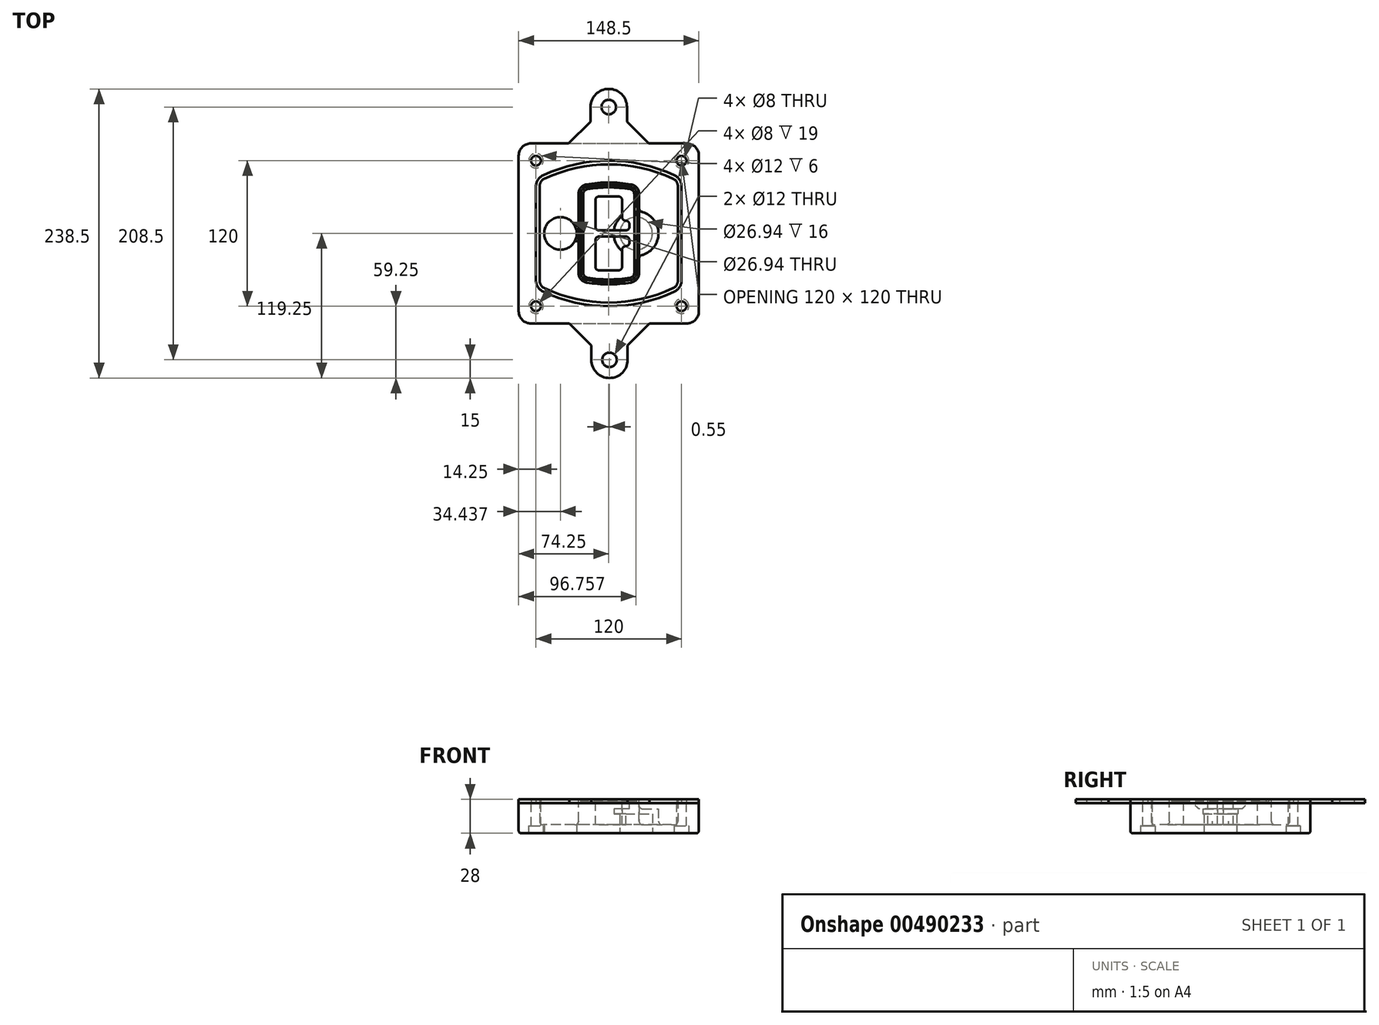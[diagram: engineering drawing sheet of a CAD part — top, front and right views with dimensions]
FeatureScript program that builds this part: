
annotation { "Feature Type Name" : "Feature", "Feature Type Description" : "" }
export const myFeature = defineFeature(function(context is Context, id is Id, definition is map)
    precondition{}
    {
        {
            var Q0;
            Q0=qCreatedBy(makeId("Top.planeOp"),FACE);
            var sketch = newSketch(context, id + "F0", { "sketchPlane" : qUnion([Q0])});
            skPoint(sketch, "E0.rect.middle", {"position": v(0, 0) * mm});
            skLineSegment(sketch, "E1.bottom", {"start": v(-64.25, -74.25) * mm, "end": v(64.25, -74.25) * mm});
            skLineSegment(sketch, "E1.top", {"start": v(-64.25, 74.25) * mm, "end": v(64.25, 74.25) * mm});
            skLineSegment(sketch, "E1.left", {"start": v(-74.25, -64.25) * mm, "end": v(-74.25, 64.25) * mm});
            skLineSegment(sketch, "E1.right", {"start": v(74.25, -64.25) * mm, "end": v(74.25, 64.25) * mm});
            skLineSegment(sketch, "E2", {"start": v(-74.25, 74.25) * mm, "end": v(74.25, -74.25) * mm, "construction": true});
            skLineSegment(sketch, "E3", {"start": v(74.25, 74.25) * mm, "end": v(-74.25, -74.25) * mm, "construction": true});
            skCircle(sketch, "E4", {"center": v(-60, 60) * mm, "radius": 4 * mm});
            skCircle(sketch, "E5", {"center": v(60, 60) * mm, "radius": 4 * mm});
            skCircle(sketch, "E6", {"center": v(60, -60) * mm, "radius": 4 * mm});
            skCircle(sketch, "E7", {"center": v(-60, -60) * mm, "radius": 4 * mm});
            skLineSegment(sketch, "E8", {"start": v(-60, 60) * mm, "end": v(60, 60) * mm, "construction": true});
            skLineSegment(sketch, "E9", {"start": v(60, 60) * mm, "end": v(60, -60) * mm, "construction": true});
            skLineSegment(sketch, "E10", {"start": v(60, -60) * mm, "end": v(-60, -60) * mm, "construction": true});
            skLineSegment(sketch, "E11", {"start": v(-60, -60) * mm, "end": v(-60, 60) * mm, "construction": true});
            skLineSegment(sketch, "E12", {"start": v(-60, 38.83) * mm, "end": v(-60, -38.83) * mm});
            skLineSegment(sketch, "E13", {"start": v(60, 38.83) * mm, "end": v(60, -38.83) * mm});
            skArc(sketch, "E14", {"start": v(54.26, 47.88) * mm, "mid": v(0, 60) * mm, "end": v(-54.26, 47.88) * mm});
            skArc(sketch, "E15", {"start": v(-54.26, -47.88) * mm, "mid": v(0, -60) * mm, "end": v(54.26, -47.88) * mm});
            skLineSegment(sketch, "E16", {"start": v(-60, 0) * mm, "end": v(60, 0) * mm, "construction": true});
            skPoint(sketch, "E17.visualSharp", {"position": v(-60, -45) * mm});
            skArc(sketch, "E17.filletArc", {"start": v(-60, -38.83) * mm, "mid": v(-58.44, -44.2) * mm, "end": v(-54.26, -47.88) * mm});
            skPoint(sketch, "E18.visualSharp", {"position": v(-60, 45) * mm});
            skArc(sketch, "E18.filletArc", {"start": v(-54.26, 47.88) * mm, "mid": v(-58.44, 44.2) * mm, "end": v(-60, 38.83) * mm});
            skPoint(sketch, "E19.visualSharp", {"position": v(60, 45) * mm});
            skArc(sketch, "E19.filletArc", {"start": v(60, 38.83) * mm, "mid": v(58.44, 44.2) * mm, "end": v(54.26, 47.88) * mm});
            skPoint(sketch, "E20.visualSharp", {"position": v(60, -45) * mm});
            skArc(sketch, "E20.filletArc", {"start": v(54.26, -47.88) * mm, "mid": v(58.44, -44.2) * mm, "end": v(60, -38.83) * mm});
            skPoint(sketch, "E21.visualSharp", {"position": v(-74.25, 74.25) * mm});
            skArc(sketch, "E21.filletArc", {"start": v(-64.25, 74.25) * mm, "mid": v(-71.32, 71.32) * mm, "end": v(-74.25, 64.25) * mm});
            skPoint(sketch, "E22.visualSharp", {"position": v(74.25, 74.25) * mm});
            skArc(sketch, "E22.filletArc", {"start": v(74.25, 64.25) * mm, "mid": v(71.32, 71.32) * mm, "end": v(64.25, 74.25) * mm});
            skPoint(sketch, "E23.visualSharp", {"position": v(74.25, -74.25) * mm});
            skArc(sketch, "E23.filletArc", {"start": v(64.25, -74.25) * mm, "mid": v(71.32, -71.32) * mm, "end": v(74.25, -64.25) * mm});
            skPoint(sketch, "E24.visualSharp", {"position": v(-74.25, -74.25) * mm});
            skArc(sketch, "E24.filletArc", {"start": v(-74.25, -64.25) * mm, "mid": v(-71.32, -71.32) * mm, "end": v(-64.25, -74.25) * mm});
            skArc(sketch, "E25.0", {"start": v(57, 38.83) * mm, "mid": v(55.9, 42.58) * mm, "end": v(52.98, 45.17) * mm});
            skLineSegment(sketch, "E25.1", {"start": v(57, 38.83) * mm, "end": v(57, -38.83) * mm});
            skArc(sketch, "E25.2", {"start": v(52.98, -45.17) * mm, "mid": v(55.9, -42.58) * mm, "end": v(57, -38.83) * mm});
            skArc(sketch, "E25.3", {"start": v(-52.98, -45.17) * mm, "mid": v(0, -57) * mm, "end": v(52.98, -45.17) * mm});
            skArc(sketch, "E25.4", {"start": v(-57, -38.83) * mm, "mid": v(-55.9, -42.58) * mm, "end": v(-52.98, -45.17) * mm});
            skArc(sketch, "E25.5", {"start": v(52.98, 45.17) * mm, "mid": v(0, 57) * mm, "end": v(-52.98, 45.17) * mm});
            skLineSegment(sketch, "E25.6", {"start": v(-57, 38.83) * mm, "end": v(-57, -38.83) * mm});
            skArc(sketch, "E25.7", {"start": v(-52.98, 45.17) * mm, "mid": v(-55.9, 42.58) * mm, "end": v(-57, 38.83) * mm});
            skArc(sketch, "E26.0", {"start": v(-55.96, 51.5) * mm, "mid": v(-61.82, 46.33) * mm, "end": v(-64, 38.83) * mm});
            skArc(sketch, "E26.1", {"start": v(55.96, 51.5) * mm, "mid": v(0, 64) * mm, "end": v(-55.96, 51.5) * mm});
            skArc(sketch, "E26.2", {"start": v(64, 38.83) * mm, "mid": v(61.82, 46.33) * mm, "end": v(55.96, 51.5) * mm});
            skLineSegment(sketch, "E26.3", {"start": v(64, 38.83) * mm, "end": v(64, -38.83) * mm});
            skArc(sketch, "E26.4", {"start": v(55.96, -51.5) * mm, "mid": v(61.82, -46.33) * mm, "end": v(64, -38.83) * mm});
            skLineSegment(sketch, "E26.5", {"start": v(-64, 38.83) * mm, "end": v(-64, -38.83) * mm});
            skArc(sketch, "E26.6", {"start": v(-55.96, -51.5) * mm, "mid": v(0, -64) * mm, "end": v(55.96, -51.5) * mm});
            skArc(sketch, "E26.7", {"start": v(-64, -38.83) * mm, "mid": v(-61.82, -46.33) * mm, "end": v(-55.96, -51.5) * mm});
            skSolve(sketch);
        }
        {
            var Q0;
            Q0=makeQuery(id+"F0.imprint","IMPRINT",FACE,{"disambiguationData":[TD([[makeQuery(id+"F0.imprint","IMPRINT",EDGE,{"derivedFrom":sQuery(id+"F0.wireOp",EDGE,"E1.bottom")}),1.0]])]});
            var Q1;
            Q1=makeQuery(id+"F0.imprint","IMPRINT",FACE,{"disambiguationData":[TD([[makeQuery(id+"F0.imprint","IMPRINT",EDGE,{"derivedFrom":sQuery(id+"F0.wireOp",EDGE,"E12")}),1.0]])]});
            var Q2;
            Q2=makeQuery(id+"F0.imprint","IMPRINT",FACE,{"disambiguationData":[TD([[makeQuery(id+"F0.imprint","IMPRINT",EDGE,{"derivedFrom":sQuery(id+"F0.wireOp",EDGE,"E25.0")}),1.0]])]});
            var Q3;
            Q3=makeQuery(id+"F0.imprint","IMPRINT",FACE,{"disambiguationData":[TD([[makeQuery(id+"F0.imprint","IMPRINT",EDGE,{"derivedFrom":sQuery(id+"F0.wireOp",EDGE,"E12")}),-1.0]])]});
            extrude(context, id + "F1", {"entities" : qUnion([Q0, Q1, Q2, Q3]), "oppositeDirection" : true, "depth" : 25 * mm});
        }
        {
            var Q0;
            Q0=makeQuery(id+"F0.imprint","IMPRINT",FACE,{"disambiguationData":[TD([[makeQuery(id+"F0.imprint","IMPRINT",EDGE,{"derivedFrom":sQuery(id+"F0.wireOp",EDGE,"E12")}),1.0]])]});
            extrude(context, id + "F2", {"entities" : qUnion([Q0]), "operationType" : NewBodyOperationType.ADD, "depth" : 3 * mm});
        }
        {
            var Q0;
            Q0=makeQuery(id+"F0.imprint","IMPRINT",FACE,{"disambiguationData":[TD([[makeQuery(id+"F0.imprint","IMPRINT",EDGE,{"derivedFrom":sQuery(id+"F0.wireOp",EDGE,"E25.0")}),1.0]])]});
            extrude(context, id + "F3", {"entities" : qUnion([Q0]), "operationType" : NewBodyOperationType.REMOVE, "oppositeDirection" : true, "depth" : 18 * mm});
        }
        {
            var Q0;
            Q0=makeQuery(id+"F2.opExtrude","CAP_FACE",FACE,{"disambiguationData":[OSD([sQuery(id+"F0.wireOp",EDGE,"E12"),sQuery(id+"F0.wireOp",EDGE,"E13"),sQuery(id+"F0.wireOp",EDGE,"E14"),sQuery(id+"F0.wireOp",EDGE,"E15"),sQuery(id+"F0.wireOp",EDGE,"E17.filletArc"),sQuery(id+"F0.wireOp",EDGE,"E18.filletArc"),sQuery(id+"F0.wireOp",EDGE,"E19.filletArc"),sQuery(id+"F0.wireOp",EDGE,"E20.filletArc"),sQuery(id+"F0.wireOp",EDGE,"E25.0"),sQuery(id+"F0.wireOp",EDGE,"E25.1"),sQuery(id+"F0.wireOp",EDGE,"E25.2"),sQuery(id+"F0.wireOp",EDGE,"E25.3"),sQuery(id+"F0.wireOp",EDGE,"E25.4"),sQuery(id+"F0.wireOp",EDGE,"E25.5"),sQuery(id+"F0.wireOp",EDGE,"E25.6"),sQuery(id+"F0.wireOp",EDGE,"E25.7")])],"isStart":false});
            var sketch = newSketch(context, id + "F4", { "sketchPlane" : qUnion([Q0])});
            skArc(sketch, "E27.0", {"start": v(-18.34, -40.45) * mm, "mid": v(0, -42) * mm, "end": v(18.34, -40.45) * mm});
            skArc(sketch, "E28.0", {"start": v(18.34, 40.45) * mm, "mid": v(0, 42) * mm, "end": v(-18.34, 40.45) * mm});
            skLineSegment(sketch, "E29", {"start": v(-25, 32.57) * mm, "end": v(-25, -32.57) * mm});
            skLineSegment(sketch, "E30", {"start": v(25, 32.57) * mm, "end": v(25, -32.57) * mm});
            skLineSegment(sketch, "E31", {"start": v(-25, 39.1) * mm, "end": v(25, 39.1) * mm, "construction": true});
            skLineSegment(sketch, "E32", {"start": v(-25, -39.1) * mm, "end": v(25, -39.1) * mm, "construction": true});
            skPoint(sketch, "E33.visualSharp", {"position": v(-25, 39.1) * mm});
            skArc(sketch, "E33.filletArc", {"start": v(-18.34, 40.45) * mm, "mid": v(-23.11, 37.73) * mm, "end": v(-25, 32.57) * mm});
            skPoint(sketch, "E34.visualSharp", {"position": v(25, 39.1) * mm});
            skArc(sketch, "E34.filletArc", {"start": v(25, 32.57) * mm, "mid": v(23.11, 37.73) * mm, "end": v(18.34, 40.45) * mm});
            skPoint(sketch, "E35.visualSharp", {"position": v(25, -39.1) * mm});
            skArc(sketch, "E35.filletArc", {"start": v(18.34, -40.45) * mm, "mid": v(23.11, -37.73) * mm, "end": v(25, -32.57) * mm});
            skPoint(sketch, "E36.visualSharp", {"position": v(-25, -39.1) * mm});
            skArc(sketch, "E36.filletArc", {"start": v(-25, -32.57) * mm, "mid": v(-23.11, -37.73) * mm, "end": v(-18.34, -40.45) * mm});
            skArc(sketch, "E37.0", {"start": v(52.98, 45.17) * mm, "mid": v(0, 57) * mm, "end": v(-52.98, 45.17) * mm});
            skArc(sketch, "E37.1", {"start": v(-52.98, 45.17) * mm, "mid": v(-55.9, 42.58) * mm, "end": v(-57, 38.83) * mm});
            skLineSegment(sketch, "E37.2", {"start": v(-57, 38.83) * mm, "end": v(-57, -38.83) * mm});
            skArc(sketch, "E37.3", {"start": v(-57, -38.83) * mm, "mid": v(-55.9, -42.58) * mm, "end": v(-52.98, -45.17) * mm});
            skArc(sketch, "E37.4", {"start": v(-52.98, -45.17) * mm, "mid": v(0, -57) * mm, "end": v(52.98, -45.17) * mm});
            skArc(sketch, "E37.5", {"start": v(52.98, -45.17) * mm, "mid": v(55.9, -42.58) * mm, "end": v(57, -38.83) * mm});
            skLineSegment(sketch, "E37.6", {"start": v(57, 38.83) * mm, "end": v(57, -38.83) * mm});
            skArc(sketch, "E37.7", {"start": v(57, 38.83) * mm, "mid": v(55.9, 42.58) * mm, "end": v(52.98, 45.17) * mm});
            skLineSegment(sketch, "E38.0", {"start": v(23, 32.57) * mm, "end": v(23, -32.57) * mm});
            skArc(sketch, "E38.1", {"start": v(18, -38.48) * mm, "mid": v(21.58, -36.44) * mm, "end": v(23, -32.57) * mm});
            skArc(sketch, "E38.2", {"start": v(-18, -38.48) * mm, "mid": v(0, -40) * mm, "end": v(18, -38.48) * mm});
            skArc(sketch, "E38.3", {"start": v(-23, -32.57) * mm, "mid": v(-21.58, -36.44) * mm, "end": v(-18, -38.48) * mm});
            skLineSegment(sketch, "E38.4", {"start": v(-23, 32.57) * mm, "end": v(-23, -32.57) * mm});
            skArc(sketch, "E38.5", {"start": v(23, 32.57) * mm, "mid": v(21.58, 36.44) * mm, "end": v(18, 38.48) * mm});
            skArc(sketch, "E38.6", {"start": v(-18, 38.48) * mm, "mid": v(-21.58, 36.44) * mm, "end": v(-23, 32.57) * mm});
            skArc(sketch, "E38.7", {"start": v(18, 38.48) * mm, "mid": v(0, 40) * mm, "end": v(-18, 38.48) * mm});
            skArc(sketch, "E39.0", {"start": v(21, 32.57) * mm, "mid": v(20.06, 35.15) * mm, "end": v(17.67, 36.5) * mm});
            skLineSegment(sketch, "E39.1", {"start": v(21, 32.57) * mm, "end": v(21, -32.57) * mm});
            skArc(sketch, "E39.2", {"start": v(17.67, -36.5) * mm, "mid": v(20.06, -35.15) * mm, "end": v(21, -32.57) * mm});
            skArc(sketch, "E39.3", {"start": v(-17.67, -36.5) * mm, "mid": v(0, -38) * mm, "end": v(17.67, -36.5) * mm});
            skArc(sketch, "E39.4", {"start": v(-21, -32.57) * mm, "mid": v(-20.06, -35.15) * mm, "end": v(-17.67, -36.5) * mm});
            skArc(sketch, "E39.5", {"start": v(17.67, 36.5) * mm, "mid": v(0, 38) * mm, "end": v(-17.67, 36.5) * mm});
            skLineSegment(sketch, "E39.6", {"start": v(-21, 32.57) * mm, "end": v(-21, -32.57) * mm});
            skArc(sketch, "E39.7", {"start": v(-17.67, 36.5) * mm, "mid": v(-20.06, 35.15) * mm, "end": v(-21, 32.57) * mm});
            skLineSegment(sketch, "E40", {"start": v(-25, 0) * mm, "end": v(25, 0) * mm, "construction": true});
            skLineSegment(sketch, "E41", {"start": v(-11, 5.5) * mm, "end": v(-11, 27.5) * mm});
            skLineSegment(sketch, "E42", {"start": v(-8, 30.5) * mm, "end": v(8, 30.5) * mm});
            skLineSegment(sketch, "E43", {"start": v(11, 27.5) * mm, "end": v(11, 13.5) * mm});
            skLineSegment(sketch, "E44", {"start": v(14, 10.5) * mm, "end": v(14, 10.5) * mm});
            skLineSegment(sketch, "E45", {"start": v(17, 7.5) * mm, "end": v(17, 5.5) * mm});
            skLineSegment(sketch, "E46", {"start": v(14, 2.5) * mm, "end": v(-8, 2.5) * mm});
            skPoint(sketch, "E47.visualSharp", {"position": v(-11, 30.5) * mm});
            skArc(sketch, "E47.filletArc", {"start": v(-8, 30.5) * mm, "mid": v(-10.12, 29.62) * mm, "end": v(-11, 27.5) * mm});
            skPoint(sketch, "E48.visualSharp", {"position": v(11, 30.5) * mm});
            skArc(sketch, "E48.filletArc", {"start": v(11, 27.5) * mm, "mid": v(10.12, 29.62) * mm, "end": v(8, 30.5) * mm});
            skPoint(sketch, "E49.visualSharp", {"position": v(11, 10.5) * mm});
            skArc(sketch, "E49.filletArc", {"start": v(11, 13.5) * mm, "mid": v(11.88, 11.38) * mm, "end": v(14, 10.5) * mm});
            skPoint(sketch, "E50.visualSharp", {"position": v(17, 10.5) * mm});
            skArc(sketch, "E50.filletArc", {"start": v(17, 7.5) * mm, "mid": v(16.12, 9.62) * mm, "end": v(14, 10.5) * mm});
            skPoint(sketch, "E51.visualSharp", {"position": v(17, 2.5) * mm});
            skArc(sketch, "E51.filletArc", {"start": v(14, 2.5) * mm, "mid": v(16.12, 3.38) * mm, "end": v(17, 5.5) * mm});
            skPoint(sketch, "E52.visualSharp", {"position": v(-11, 2.5) * mm});
            skArc(sketch, "E52.filletArc", {"start": v(-11, 5.5) * mm, "mid": v(-10.12, 3.38) * mm, "end": v(-8, 2.5) * mm});
            skLineSegment(sketch, "E53.0.MirrorCS", {"start": v(14, -2.5) * mm, "end": v(-8, -2.5) * mm});
            skArc(sketch, "E54.0.MirrorCS", {"start": v(-11, -5.5) * mm, "mid": v(-10.12, -3.38) * mm, "end": v(-8, -2.5) * mm});
            skLineSegment(sketch, "E55.0.MirrorCS", {"start": v(-11, -5.5) * mm, "end": v(-11, -27.5) * mm});
            skArc(sketch, "E56.0.MirrorCS", {"start": v(-8, -30.5) * mm, "mid": v(-10.12, -29.62) * mm, "end": v(-11, -27.5) * mm});
            skLineSegment(sketch, "E57.0.MirrorCS", {"start": v(-8, -30.5) * mm, "end": v(8, -30.5) * mm});
            skArc(sketch, "E58.0.MirrorCS", {"start": v(11, -27.5) * mm, "mid": v(10.12, -29.62) * mm, "end": v(8, -30.5) * mm});
            skLineSegment(sketch, "E59.0.MirrorCS", {"start": v(11, -27.5) * mm, "end": v(11, -13.5) * mm});
            skArc(sketch, "E60.0.MirrorCS", {"start": v(11, -13.5) * mm, "mid": v(11.88, -11.38) * mm, "end": v(14, -10.5) * mm});
            skArc(sketch, "E61.0.MirrorCS", {"start": v(17, -7.5) * mm, "mid": v(16.12, -9.62) * mm, "end": v(14, -10.5) * mm});
            skLineSegment(sketch, "E62.0.MirrorCS", {"start": v(17, -7.5) * mm, "end": v(17, -5.5) * mm});
            skArc(sketch, "E63.0.MirrorCS", {"start": v(14, -2.5) * mm, "mid": v(16.12, -3.38) * mm, "end": v(17, -5.5) * mm});
            skSolve(sketch);
        }
        {
            var Q0;
            Q0=makeQuery(id+"F4.imprint","IMPRINT",FACE,{"disambiguationData":[TD([[makeQuery(id+"F4.imprint","IMPRINT",EDGE,{"derivedFrom":sQuery(id+"F4.wireOp",EDGE,"E27.0")}),1.0]])]});
            var Q1;
            Q1=makeQuery(id+"F4.imprint","IMPRINT",FACE,{"disambiguationData":[TD([[makeQuery(id+"F4.imprint","IMPRINT",EDGE,{"derivedFrom":sQuery(id+"F4.wireOp",EDGE,"E38.0")}),-1.0]])]});
            var Q2;
            Q2=makeQuery(id+"F4.imprint","IMPRINT",FACE,{"disambiguationData":[TD([[makeQuery(id+"F4.imprint","IMPRINT",EDGE,{"derivedFrom":sQuery(id+"F4.wireOp",EDGE,"E39.0")}),1.0]])]});
            extrude(context, id + "F5", {"entities" : qUnion([Q0, Q1, Q2]), "operationType" : NewBodyOperationType.ADD, "endBound" : BoundingType.UP_TO_NEXT, "oppositeDirection" : true, "depth" : 25 * mm});
        }
        {
            var Q0;
            Q0=makeQuery(id+"F4.imprint","IMPRINT",FACE,{"disambiguationData":[TD([[makeQuery(id+"F4.imprint","IMPRINT",EDGE,{"derivedFrom":sQuery(id+"F4.wireOp",EDGE,"E38.0")}),-1.0]])]});
            extrude(context, id + "F6", {"entities" : qUnion([Q0]), "operationType" : NewBodyOperationType.REMOVE, "oppositeDirection" : true, "depth" : 2 * mm});
        }
        {
            var Q0;
            Q0=makeQuery(id+"F1.opExtrude","CAP_FACE",FACE,{"disambiguationData":[OSD([sQuery(id+"F0.wireOp",EDGE,"E1.bottom"),sQuery(id+"F0.wireOp",EDGE,"E1.top"),sQuery(id+"F0.wireOp",EDGE,"E1.left"),sQuery(id+"F0.wireOp",EDGE,"E1.right"),sQuery(id+"F0.wireOp",EDGE,"E4"),sQuery(id+"F0.wireOp",EDGE,"E5"),sQuery(id+"F0.wireOp",EDGE,"E6"),sQuery(id+"F0.wireOp",EDGE,"E7"),sQuery(id+"F0.wireOp",EDGE,"E21.filletArc"),sQuery(id+"F0.wireOp",EDGE,"E22.filletArc"),sQuery(id+"F0.wireOp",EDGE,"E23.filletArc"),sQuery(id+"F0.wireOp",EDGE,"E24.filletArc")])],"isStart":false});
            var sketch = newSketch(context, id + "F7", { "sketchPlane" : qUnion([Q0])});
            skCircle(sketch, "E64", {"center": v(22.5, 0) * mm, "radius": 13.47 * mm});
            skCircle(sketch, "E65", {"center": v(-39.81, 0) * mm, "radius": 13.47 * mm});
            skLineSegment(sketch, "E66", {"start": v(74.25, 0) * mm, "end": v(-74.25, 0) * mm});
            skCircle(sketch, "E67", {"center": v(22.5, 0) * mm, "radius": 18.47 * mm});
            skCircle(sketch, "E68", {"center": v(60, -60) * mm, "radius": 6 * mm});
            skCircle(sketch, "E69", {"center": v(-60, -60) * mm, "radius": 6 * mm});
            skCircle(sketch, "E70", {"center": v(-60, 60) * mm, "radius": 6 * mm});
            skCircle(sketch, "E71", {"center": v(60, 60) * mm, "radius": 6 * mm});
            skSolve(sketch);
        }
        {
            var Q0;
            {var subQ1=sQuery(id+"F7.wireOp",EDGE,"E66");var subQ4=sQuery(id+"F7.wireOp",EDGE,"E64");var subQ6=makeQuery(id+"F7.imprint","INTERSECT",VERTEX,{"disambiguationData":[OD(0.0)],"derivedFrom":[subQ4,subQ1]});Q0=makeQuery(id+"F7.imprint","IMPRINT",FACE,{"disambiguationData":[TD([[makeQuery(id+"F7.imprint","IMPRINT",EDGE,{"disambiguationData":[TD([[subQ6,-1.0]])],"derivedFrom":subQ4}),-1.0]])]});}
            var Q1;
            {var subQ0=sQuery(id+"F7.wireOp",EDGE,"E66");var subQ1=sQuery(id+"F7.wireOp",EDGE,"E64");var subQ3=makeQuery(id+"F7.imprint","INTERSECT",VERTEX,{"disambiguationData":[OD(0.0)],"derivedFrom":[subQ1,subQ0]});Q1=makeQuery(id+"F7.imprint","IMPRINT",FACE,{"disambiguationData":[TD([[makeQuery(id+"F7.imprint","IMPRINT",EDGE,{"disambiguationData":[TD([[subQ3,-1.0]])],"derivedFrom":subQ1}),1.0]])]});}
            var Q2;
            {var subQ0=sQuery(id+"F7.wireOp",EDGE,"E66");var subQ1=sQuery(id+"F7.wireOp",EDGE,"E64");var subQ3=makeQuery(id+"F7.imprint","INTERSECT",VERTEX,{"disambiguationData":[OD(0.0)],"derivedFrom":[subQ1,subQ0]});Q2=makeQuery(id+"F7.imprint","IMPRINT",FACE,{"disambiguationData":[TD([[makeQuery(id+"F7.imprint","IMPRINT",EDGE,{"disambiguationData":[TD([[subQ3,1.0]])],"derivedFrom":subQ1}),1.0]])]});}
            var Q3;
            {var subQ1=sQuery(id+"F7.wireOp",EDGE,"E66");var subQ4=sQuery(id+"F7.wireOp",EDGE,"E64");var subQ6=makeQuery(id+"F7.imprint","INTERSECT",VERTEX,{"disambiguationData":[OD(0.0)],"derivedFrom":[subQ4,subQ1]});Q3=makeQuery(id+"F7.imprint","IMPRINT",FACE,{"disambiguationData":[TD([[makeQuery(id+"F7.imprint","IMPRINT",EDGE,{"disambiguationData":[TD([[subQ6,1.0]])],"derivedFrom":subQ4}),-1.0]])]});}
            extrude(context, id + "F8", {"entities" : qUnion([Q0, Q1, Q2, Q3]), "operationType" : NewBodyOperationType.ADD, "oppositeDirection" : true, "depth" : 20 * mm});
        }
        {
            var Q0;
            {var subQ0=sQuery(id+"F7.wireOp",EDGE,"E66");var subQ1=sQuery(id+"F7.wireOp",EDGE,"E64");var subQ3=makeQuery(id+"F7.imprint","INTERSECT",VERTEX,{"disambiguationData":[OD(0.0)],"derivedFrom":[subQ1,subQ0]});Q0=makeQuery(id+"F7.imprint","IMPRINT",FACE,{"disambiguationData":[TD([[makeQuery(id+"F7.imprint","IMPRINT",EDGE,{"disambiguationData":[TD([[subQ3,-1.0]])],"derivedFrom":subQ1}),1.0]])]});}
            var Q1;
            {var subQ0=sQuery(id+"F7.wireOp",EDGE,"E66");var subQ1=sQuery(id+"F7.wireOp",EDGE,"E64");var subQ3=makeQuery(id+"F7.imprint","INTERSECT",VERTEX,{"disambiguationData":[OD(0.0)],"derivedFrom":[subQ1,subQ0]});Q1=makeQuery(id+"F7.imprint","IMPRINT",FACE,{"disambiguationData":[TD([[makeQuery(id+"F7.imprint","IMPRINT",EDGE,{"disambiguationData":[TD([[subQ3,1.0]])],"derivedFrom":subQ1}),1.0]])]});}
            extrude(context, id + "F9", {"entities" : qUnion([Q0, Q1]), "operationType" : NewBodyOperationType.REMOVE, "oppositeDirection" : true, "depth" : 16 * mm});
        }
        {
            var Q0;
            {var subQ0=sQuery(id+"F7.wireOp",EDGE,"E66");var subQ1=sQuery(id+"F7.wireOp",EDGE,"E65");var subQ3=makeQuery(id+"F7.imprint","INTERSECT",VERTEX,{"disambiguationData":[OD(0.0)],"derivedFrom":[subQ1,subQ0]});Q0=makeQuery(id+"F7.imprint","IMPRINT",FACE,{"disambiguationData":[TD([[makeQuery(id+"F7.imprint","IMPRINT",EDGE,{"disambiguationData":[TD([[subQ3,-1.0]])],"derivedFrom":subQ1}),1.0]])]});}
            var Q1;
            {var subQ0=sQuery(id+"F7.wireOp",EDGE,"E66");var subQ1=sQuery(id+"F7.wireOp",EDGE,"E65");var subQ3=makeQuery(id+"F7.imprint","INTERSECT",VERTEX,{"disambiguationData":[OD(0.0)],"derivedFrom":[subQ1,subQ0]});Q1=makeQuery(id+"F7.imprint","IMPRINT",FACE,{"disambiguationData":[TD([[makeQuery(id+"F7.imprint","IMPRINT",EDGE,{"disambiguationData":[TD([[subQ3,1.0]])],"derivedFrom":subQ1}),1.0]])]});}
            extrude(context, id + "F10", {"entities" : qUnion([Q0, Q1]), "operationType" : NewBodyOperationType.REMOVE, "oppositeDirection" : true, "depth" : 25 * mm});
        }
        {
            var Q0;
            Q0=makeQuery(id+"F7.imprint","IMPRINT",FACE,{"disambiguationData":[TD([[makeQuery(id+"F7.imprint","IMPRINT",EDGE,{"derivedFrom":sQuery(id+"F7.wireOp",EDGE,"E68")}),1.0]])]});
            var Q1;
            Q1=makeQuery(id+"F7.imprint","IMPRINT",FACE,{"disambiguationData":[TD([[makeQuery(id+"F7.imprint","IMPRINT",EDGE,{"derivedFrom":makeQuery(id+"F1.opExtrude","CAP_EDGE",EDGE,{"disambiguationData":[OSD([sQuery(id+"F0.wireOp",EDGE,"E5")])],"isStart":false})}),-1.0]])]});
            var Q2;
            Q2=makeQuery(id+"F7.imprint","IMPRINT",FACE,{"disambiguationData":[TD([[makeQuery(id+"F7.imprint","IMPRINT",EDGE,{"derivedFrom":sQuery(id+"F7.wireOp",EDGE,"E69")}),1.0]])]});
            var Q3;
            Q3=makeQuery(id+"F7.imprint","IMPRINT",FACE,{"disambiguationData":[TD([[makeQuery(id+"F7.imprint","IMPRINT",EDGE,{"derivedFrom":makeQuery(id+"F1.opExtrude","CAP_EDGE",EDGE,{"disambiguationData":[OSD([sQuery(id+"F0.wireOp",EDGE,"E4")])],"isStart":false})}),-1.0]])]});
            var Q4;
            Q4=makeQuery(id+"F7.imprint","IMPRINT",FACE,{"disambiguationData":[TD([[makeQuery(id+"F7.imprint","IMPRINT",EDGE,{"derivedFrom":sQuery(id+"F7.wireOp",EDGE,"E70")}),1.0]])]});
            var Q5;
            Q5=makeQuery(id+"F7.imprint","IMPRINT",FACE,{"disambiguationData":[TD([[makeQuery(id+"F7.imprint","IMPRINT",EDGE,{"derivedFrom":makeQuery(id+"F1.opExtrude","CAP_EDGE",EDGE,{"disambiguationData":[OSD([sQuery(id+"F0.wireOp",EDGE,"E7")])],"isStart":false})}),-1.0]])]});
            var Q6;
            Q6=makeQuery(id+"F7.imprint","IMPRINT",FACE,{"disambiguationData":[TD([[makeQuery(id+"F7.imprint","IMPRINT",EDGE,{"derivedFrom":sQuery(id+"F7.wireOp",EDGE,"E71")}),1.0]])]});
            var Q7;
            Q7=makeQuery(id+"F7.imprint","IMPRINT",FACE,{"disambiguationData":[TD([[makeQuery(id+"F7.imprint","IMPRINT",EDGE,{"derivedFrom":makeQuery(id+"F1.opExtrude","CAP_EDGE",EDGE,{"disambiguationData":[OSD([sQuery(id+"F0.wireOp",EDGE,"E6")])],"isStart":false})}),-1.0]])]});
            extrude(context, id + "F11", {"entities" : qUnion([Q0, Q1, Q2, Q3, Q4, Q5, Q6, Q7]), "operationType" : NewBodyOperationType.REMOVE, "oppositeDirection" : true, "depth" : 6 * mm});
        }
        {
            var Q0;
            Q0=makeQuery(id+"F9.boolean.opBoolean","COPY",FACE,{"derivedFrom":makeQuery(id+"F9.opExtrude","CAP_FACE",FACE,{"disambiguationData":[OSD([sQuery(id+"F7.wireOp",EDGE,"E64")])],"isStart":false})});
            var sketch = newSketch(context, id + "F12", { "sketchPlane" : qUnion([Q0])});
            skArc(sketch, "E72.0", {"start": v(11, 14.45) * mm, "mid": v(6.45, 9.13) * mm, "end": v(4.2, 2.5) * mm});
            skArc(sketch, "E72.1", {"start": v(4.2, -2.5) * mm, "mid": v(6.45, -9.13) * mm, "end": v(11, -14.45) * mm});
            skLineSegment(sketch, "E73", {"start": v(4.2, -2.5) * mm, "end": v(14, -2.5) * mm});
            skLineSegment(sketch, "E74.0", {"start": v(14, 2.5) * mm, "end": v(4.2, 2.5) * mm});
            skArc(sketch, "E74.1", {"start": v(14, 2.5) * mm, "mid": v(16.12, 3.38) * mm, "end": v(17, 5.5) * mm});
            skLineSegment(sketch, "E74.2", {"start": v(17, 7.5) * mm, "end": v(17, 5.5) * mm});
            skArc(sketch, "E74.3", {"start": v(17, 7.5) * mm, "mid": v(16.12, 9.62) * mm, "end": v(14, 10.5) * mm});
            skArc(sketch, "E74.4", {"start": v(11, 13.5) * mm, "mid": v(11.88, 11.38) * mm, "end": v(14, 10.5) * mm});
            skLineSegment(sketch, "E74.5", {"start": v(11, 14.45) * mm, "end": v(11, 13.5) * mm});
            skLineSegment(sketch, "E74.7", {"start": v(14, -2.5) * mm, "end": v(4.2, -2.5) * mm});
            skArc(sketch, "E74.8", {"start": v(14, -2.5) * mm, "mid": v(16.12, -3.38) * mm, "end": v(17, -5.5) * mm});
            skLineSegment(sketch, "E74.9", {"start": v(17, -7.5) * mm, "end": v(17, -5.5) * mm});
            skArc(sketch, "E74.10", {"start": v(17, -7.5) * mm, "mid": v(16.12, -9.62) * mm, "end": v(14, -10.5) * mm});
            skArc(sketch, "E74.11", {"start": v(11, -13.5) * mm, "mid": v(11.88, -11.38) * mm, "end": v(14, -10.5) * mm});
            skLineSegment(sketch, "E74.12", {"start": v(11, -14.45) * mm, "end": v(11, -13.5) * mm});
            skPoint(sketch, "E75.orphan", {"position": v(11, -27.5) * mm});
            skPoint(sketch, "E76.orphan", {"position": v(-8, -2.5) * mm});
            skPoint(sketch, "E77.orphan", {"position": v(-8, 2.5) * mm});
            skPoint(sketch, "E78.orphan", {"position": v(11, 27.5) * mm});
            skSolve(sketch);
        }
        {
            var Q0;
            {var subQ7=sQuery(id+"F12.wireOp",EDGE,"E72.0");var subQ14=sQuery(id+"F12.wireOp",EDGE,"E72.1");var subQ16=sQuery(id+"F12.wireOp",EDGE,"E74.1");var subQ18=sQuery(id+"F12.wireOp",EDGE,"E74.8");Q0=qUnion([makeQuery(id+"F12.imprint","IMPRINT",FACE,{"disambiguationData":[TD([[makeQuery(id+"F12.imprint","IMPRINT",EDGE,{"derivedFrom":subQ7}),1.0]])]}),makeQuery(id+"F12.imprint","IMPRINT",FACE,{"disambiguationData":[TD([[makeQuery(id+"F12.imprint","IMPRINT",EDGE,{"derivedFrom":subQ14}),1.0]])]}),makeQuery(id+"F12.imprint","IMPRINT",FACE,{"disambiguationData":[TD([[makeQuery(id+"F12.imprint","IMPRINT",EDGE,{"derivedFrom":subQ16}),1.0]])]}),makeQuery(id+"F12.imprint","IMPRINT",FACE,{"disambiguationData":[TD([[makeQuery(id+"F12.imprint","IMPRINT",EDGE,{"derivedFrom":subQ18}),-1.0]])]})]);}
            var Q1;
            Q1=makeQuery(id+"F5.boolean.opBoolean","SPLIT",FACE,{"disambiguationData":[TD([makeQuery(id+"F5.opExtrude","SWEPT_FACE",FACE,{"disambiguationData":[OSD([sQuery(id+"F4.wireOp",EDGE,"E41")])]})])],"derivedFrom":makeQuery(id+"F3.boolean.opBoolean","COPY",FACE,{"derivedFrom":makeQuery(id+"F3.opExtrude","CAP_FACE",FACE,{"disambiguationData":[OSD([sQuery(id+"F0.wireOp",EDGE,"E25.0"),sQuery(id+"F0.wireOp",EDGE,"E25.1"),sQuery(id+"F0.wireOp",EDGE,"E25.2"),sQuery(id+"F0.wireOp",EDGE,"E25.3"),sQuery(id+"F0.wireOp",EDGE,"E25.4"),sQuery(id+"F0.wireOp",EDGE,"E25.5"),sQuery(id+"F0.wireOp",EDGE,"E25.6"),sQuery(id+"F0.wireOp",EDGE,"E25.7")])],"isStart":false})})});
            extrude(context, id + "F13", {"entities" : qUnion([Q0]), "operationType" : NewBodyOperationType.REMOVE, "endBound" : BoundingType.UP_TO_SURFACE, "endBoundEntityFace" : qUnion([Q1]), "depth" : 25 * mm});
        }
        {
            var Q0;
            Q0=makeQuery(id+"F3.boolean.opBoolean","COPY",EDGE,{"derivedFrom":makeQuery(id+"F3.opExtrude","CAP_EDGE",EDGE,{"disambiguationData":[OSD([sQuery(id+"F0.wireOp",EDGE,"E25.6")])],"isStart":false})});
            var Q1;
            Q1=makeQuery(id+"F8.boolean.opBoolean","INTERSECT",EDGE,{"derivedFrom":[makeQuery(id+"F5.opExtrude","SWEPT_FACE",FACE,{"disambiguationData":[OSD([sQuery(id+"F4.wireOp",EDGE,"E30")])]}),makeQuery(id+"F8.opExtrude","CAP_FACE",FACE,{"disambiguationData":[OSD([sQuery(id+"F7.wireOp",EDGE,"E67")])],"isStart":false})]});
            var Q2;
            Q2=makeQuery(id+"F8.boolean.opBoolean","INTERSECT",EDGE,{"disambiguationData":[OD(1.0)],"derivedFrom":[makeQuery(id+"F5.opExtrude","SWEPT_FACE",FACE,{"disambiguationData":[OSD([sQuery(id+"F4.wireOp",EDGE,"E30")])]}),makeQuery(id+"F8.opExtrude","SWEPT_FACE",FACE,{"disambiguationData":[OSD([sQuery(id+"F7.wireOp",EDGE,"E67")])]})]});
            var Q3;
            {var subQ0=sQuery(id+"F4.wireOp",EDGE,"E30");Q3=makeQuery(id+"F8.boolean.opBoolean","SPLIT",EDGE,{"disambiguationData":[TD([makeQuery(id+"F5.opExtrude","SWEPT_FACE",FACE,{"disambiguationData":[OSD([sQuery(id+"F4.wireOp",EDGE,"E35.filletArc")])]})])],"derivedFrom":makeQuery(id+"F5.opExtrude","CAP_EDGE",EDGE,{"disambiguationData":[OSD([subQ0])],"isStart":false})});}
            var Q4;
            {var subQ0=sQuery(id+"F0.wireOp",EDGE,"E25.7");var subQ1=sQuery(id+"F0.wireOp",EDGE,"E25.1");var subQ2=sQuery(id+"F0.wireOp",EDGE,"E25.6");var subQ3=sQuery(id+"F0.wireOp",EDGE,"E25.5");var subQ4=sQuery(id+"F0.wireOp",EDGE,"E25.4");var subQ5=sQuery(id+"F0.wireOp",EDGE,"E25.0");var subQ6=sQuery(id+"F0.wireOp",EDGE,"E25.2");var subQ7=sQuery(id+"F0.wireOp",EDGE,"E25.3");Q4=makeQuery(id+"F8.boolean.opBoolean","INTERSECT",EDGE,{"derivedFrom":[makeQuery(id+"F5.boolean.opBoolean","SPLIT",FACE,{"disambiguationData":[TD([makeQuery(id+"F2.opExtrude","SWEPT_FACE",FACE,{"disambiguationData":[OSD([subQ5])]})])],"derivedFrom":makeQuery(id+"F3.boolean.opBoolean","COPY",FACE,{"derivedFrom":makeQuery(id+"F3.opExtrude","CAP_FACE",FACE,{"disambiguationData":[OSD([subQ5,subQ1,subQ6,subQ7,subQ4,subQ3,subQ2,subQ0])],"isStart":false})})}),makeQuery(id+"F8.opExtrude","SWEPT_FACE",FACE,{"disambiguationData":[OSD([sQuery(id+"F7.wireOp",EDGE,"E67")])]})]});}
            var Q5;
            Q5=makeQuery(id+"F8.boolean.opBoolean","INTERSECT",EDGE,{"disambiguationData":[OD(0.0)],"derivedFrom":[makeQuery(id+"F5.opExtrude","SWEPT_FACE",FACE,{"disambiguationData":[OSD([sQuery(id+"F4.wireOp",EDGE,"E30")])]}),makeQuery(id+"F8.opExtrude","SWEPT_FACE",FACE,{"disambiguationData":[OSD([sQuery(id+"F7.wireOp",EDGE,"E67")])]})]});
            fillet(context, id + "F14", {"entities" : qUnion([Q0, Q1, Q2, Q3, Q4, Q5]), "radius" : 3 * mm, "tangentPropagation" : true, "allowEdgeOverflow" : false});
        }
        {
            var Q0;
            Q0=makeQuery(id+"F1.opExtrude","CAP_EDGE",EDGE,{"disambiguationData":[OSD([sQuery(id+"F0.wireOp",EDGE,"E1.bottom")])],"isStart":false});
            fillet(context, id + "F15", {"entities" : qUnion([Q0]), "radius" : 2 * mm, "tangentPropagation" : true, "allowEdgeOverflow" : false});
        }
        {
            var Q0;
            {var subQ0=sQuery(id+"F0.wireOp",EDGE,"E21.filletArc");var subQ1=sQuery(id+"F0.wireOp",EDGE,"E7");var subQ2=sQuery(id+"F0.wireOp",EDGE,"E6");var subQ3=sQuery(id+"F0.wireOp",EDGE,"E5");var subQ4=sQuery(id+"F0.wireOp",EDGE,"E4");var subQ5=sQuery(id+"F0.wireOp",EDGE,"E22.filletArc");var subQ6=sQuery(id+"F0.wireOp",EDGE,"E1.bottom");var subQ7=sQuery(id+"F0.wireOp",EDGE,"E1.right");var subQ8=sQuery(id+"F0.wireOp",EDGE,"E1.top");var subQ9=sQuery(id+"F0.wireOp",EDGE,"E1.left");var subQ10=sQuery(id+"F0.wireOp",EDGE,"E23.filletArc");var subQ11=sQuery(id+"F0.wireOp",EDGE,"E24.filletArc");Q0=makeQuery(id+"F2.boolean.opBoolean","SPLIT",FACE,{"disambiguationData":[TD([makeQuery(id+"F1.opExtrude","SWEPT_FACE",FACE,{"disambiguationData":[OSD([subQ6])]})])],"derivedFrom":makeQuery(id+"F1.opExtrude","CAP_FACE",FACE,{"disambiguationData":[OSD([subQ6,subQ8,subQ9,subQ7,subQ4,subQ3,subQ2,subQ1,subQ0,subQ5,subQ10,subQ11])],"isStart":true})});}
            var sketch = newSketch(context, id + "F16", { "sketchPlane" : qUnion([Q0])});
            skLineSegment(sketch, "E79", {"start": v(0, 74.25) * mm, "end": v(0, 104.25) * mm, "construction": true});
            skCircle(sketch, "E80", {"center": v(0, 104.25) * mm, "radius": 6 * mm});
            skArc(sketch, "E81", {"start": v(15, 104.25) * mm, "mid": v(0, 119.25) * mm, "end": v(-15, 104.25) * mm});
            skLineSegment(sketch, "E82", {"start": v(-15, 104.25) * mm, "end": v(-15, 92.25) * mm});
            skLineSegment(sketch, "E83", {"start": v(15, 104.25) * mm, "end": v(15, 92.25) * mm});
            skLineSegment(sketch, "E84", {"start": v(-15, 92.25) * mm, "end": v(-33, 74.25) * mm});
            skLineSegment(sketch, "E85", {"start": v(15, 92.25) * mm, "end": v(33, 74.25) * mm});
            skArc(sketch, "E86.MirrorC", {"start": v(-15, 104.25) * mm, "mid": v(0, 119.25) * mm, "end": v(15, 104.25) * mm});
            skLineSegment(sketch, "E87", {"start": v(0.55, -74.25) * mm, "end": v(0.55, -104.25) * mm});
            skCircle(sketch, "E88", {"center": v(0.55, -104.25) * mm, "radius": 6 * mm});
            skArc(sketch, "E89", {"start": v(-14.45, -104.25) * mm, "mid": v(0.55, -119.25) * mm, "end": v(15.55, -104.25) * mm});
            skLineSegment(sketch, "E90", {"start": v(15.55, -104.25) * mm, "end": v(15.55, -92.25) * mm});
            skLineSegment(sketch, "E91", {"start": v(-14.45, -104.25) * mm, "end": v(-14.45, -92.25) * mm});
            skLineSegment(sketch, "E92", {"start": v(15.55, -92.25) * mm, "end": v(33.55, -74.25) * mm});
            skLineSegment(sketch, "E93", {"start": v(-14.45, -92.25) * mm, "end": v(-32.45, -74.25) * mm});
            skArc(sketch, "E94.MirrorC", {"start": v(15.55, -104.25) * mm, "mid": v(0.55, -119.25) * mm, "end": v(-14.45, -104.25) * mm});
            skSolve(sketch);
        }
        {
            var Q0;
            Q0=makeQuery(id+"F16.imprint","IMPRINT",FACE,{"disambiguationData":[TD([[makeQuery(id+"F16.imprint","IMPRINT",EDGE,{"derivedFrom":sQuery(id+"F16.wireOp",EDGE,"E88")}),-1.0]])]});
            var Q1;
            Q1=makeQuery(id+"F16.imprint","IMPRINT",FACE,{"disambiguationData":[TD([[makeQuery(id+"F16.imprint","IMPRINT",EDGE,{"derivedFrom":sQuery(id+"F16.wireOp",EDGE,"E80")}),-1.0]])]});
            var Q2;
            Q2=makeQuery(id+"F16.imprint","IMPRINT",FACE,{"disambiguationData":[TD([[makeQuery(id+"F16.imprint","IMPRINT",EDGE,{"derivedFrom":makeQuery(id+"F1.opExtrude","CAP_EDGE",EDGE,{"disambiguationData":[OSD([sQuery(id+"F0.wireOp",EDGE,"E1.left")])],"isStart":true})}),-1.0]])]});
            var Q3;
            Q3=sQuery(id+"F16.wireOp",EDGE,"E92");
            var Q4;
            Q4=sQuery(id+"F16.wireOp",EDGE,"E93");
            extrude(context, id + "F17", {"entities" : qUnion([Q0, Q1, Q2]), "surfaceEntities" : qUnion([Q3, Q4]), "depth" : 3 * mm});
        }
    });
